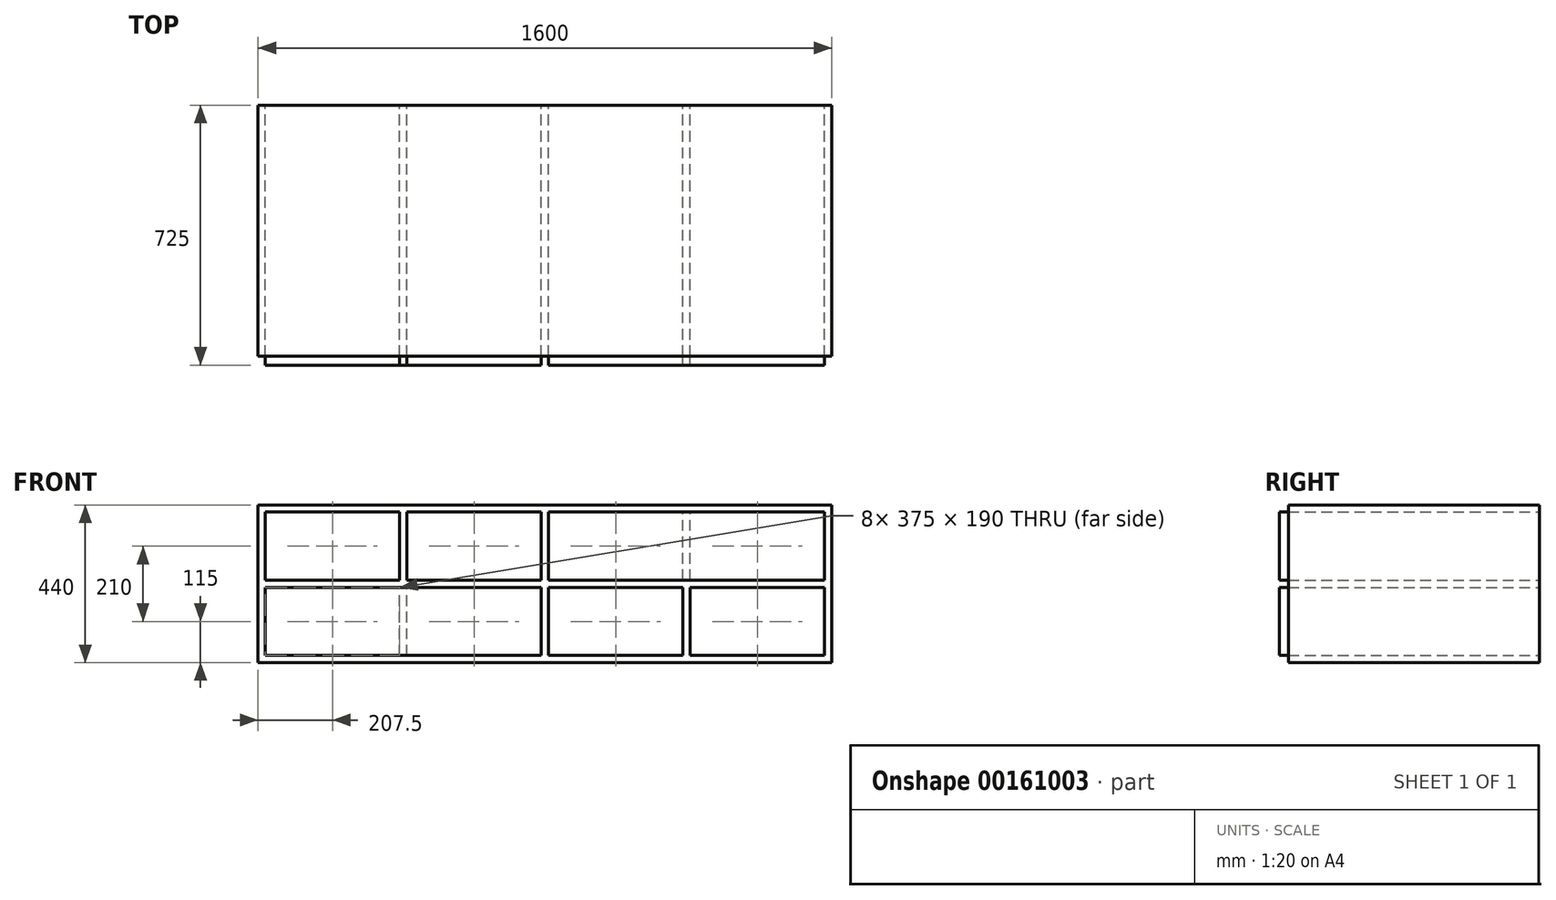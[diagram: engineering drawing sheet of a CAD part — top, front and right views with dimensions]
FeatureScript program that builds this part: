
annotation { "Feature Type Name" : "Feature", "Feature Type Description" : "" }
export const myFeature = defineFeature(function(context is Context, id is Id, definition is map)
    precondition{}
    {
        {
            var Q0;
            Q0=qCreatedBy(makeId("Front.planeOp"),FACE);
            var sketch = newSketch(context, id + "F0", { "sketchPlane" : qUnion([Q0])});
            skLineSegment(sketch, "E0.bottom", {"start": v(800, -220) * mm, "end": v(-800, -220) * mm});
            skLineSegment(sketch, "E0.top", {"start": v(800, 220) * mm, "end": v(-800, 220) * mm});
            skLineSegment(sketch, "E0.left", {"start": v(800, -220) * mm, "end": v(800, 220) * mm});
            skLineSegment(sketch, "E0.right", {"start": v(-800, -220) * mm, "end": v(-800, 220) * mm});
            skPoint(sketch, "E0.middle", {"position": v(0, 0) * mm});
            skLineSegment(sketch, "E1", {"start": v(-800, 105) * mm, "end": v(-780, 105) * mm, "construction": true});
            skLineSegment(sketch, "E2", {"start": v(-405, 105) * mm, "end": v(-385, 105) * mm, "construction": true});
            skLineSegment(sketch, "E3", {"start": v(-10, 105) * mm, "end": v(10, 105) * mm, "construction": true});
            skLineSegment(sketch, "E4", {"start": v(385, 105) * mm, "end": v(405, 105) * mm, "construction": true});
            skLineSegment(sketch, "E5", {"start": v(780, 105) * mm, "end": v(800, 105) * mm, "construction": true});
            skLineSegment(sketch, "E6", {"start": v(-800, -105) * mm, "end": v(-780, -105) * mm, "construction": true});
            skLineSegment(sketch, "E7", {"start": v(-405, -105) * mm, "end": v(-385, -105) * mm, "construction": true});
            skLineSegment(sketch, "E8", {"start": v(-10, -105) * mm, "end": v(10, -105) * mm, "construction": true});
            skLineSegment(sketch, "E9", {"start": v(385, -105) * mm, "end": v(405, -105) * mm, "construction": true});
            skLineSegment(sketch, "E10", {"start": v(780, -105) * mm, "end": v(800, -105) * mm, "construction": true});
            skLineSegment(sketch, "E11", {"start": v(-592.5, 220) * mm, "end": v(-592.5, 200) * mm, "construction": true});
            skLineSegment(sketch, "E12", {"start": v(-592.5, 10) * mm, "end": v(-592.5, -10) * mm, "construction": true});
            skLineSegment(sketch, "E13", {"start": v(-592.5, -200) * mm, "end": v(-592.5, -220) * mm, "construction": true});
            skLineSegment(sketch, "E14", {"start": v(-197.5, 220) * mm, "end": v(-197.5, 200) * mm, "construction": true});
            skLineSegment(sketch, "E15", {"start": v(-197.5, 10) * mm, "end": v(-197.5, -10) * mm, "construction": true});
            skLineSegment(sketch, "E16", {"start": v(-197.5, -200) * mm, "end": v(-197.5, -220) * mm, "construction": true});
            skLineSegment(sketch, "E17", {"start": v(197.5, 220) * mm, "end": v(197.5, 200) * mm, "construction": true});
            skLineSegment(sketch, "E18", {"start": v(197.5, 10) * mm, "end": v(197.5, -10) * mm, "construction": true});
            skLineSegment(sketch, "E19", {"start": v(197.5, -200) * mm, "end": v(197.5, -220) * mm, "construction": true});
            skLineSegment(sketch, "E20", {"start": v(592.5, 220) * mm, "end": v(592.5, 200) * mm, "construction": true});
            skLineSegment(sketch, "E21", {"start": v(592.5, 10) * mm, "end": v(592.5, -10) * mm, "construction": true});
            skLineSegment(sketch, "E22", {"start": v(592.5, -200) * mm, "end": v(592.5, -220) * mm, "construction": true});
            skLineSegment(sketch, "E23.bottom", {"start": v(-405, 10) * mm, "end": v(-780, 10) * mm});
            skLineSegment(sketch, "E23.top", {"start": v(-405, 200) * mm, "end": v(-780, 200) * mm});
            skLineSegment(sketch, "E23.left", {"start": v(-405, 10) * mm, "end": v(-405, 200) * mm});
            skLineSegment(sketch, "E23.right", {"start": v(-780, 10) * mm, "end": v(-780, 200) * mm});
            skPoint(sketch, "E23.middle", {"position": v(-592.5, 105) * mm});
            skLineSegment(sketch, "E24.bottom", {"start": v(-10, 10) * mm, "end": v(-385, 10) * mm});
            skLineSegment(sketch, "E24.top", {"start": v(-10, 200) * mm, "end": v(-385, 200) * mm});
            skLineSegment(sketch, "E24.left", {"start": v(-10, 10) * mm, "end": v(-10, 200) * mm});
            skLineSegment(sketch, "E24.right", {"start": v(-385, 10) * mm, "end": v(-385, 200) * mm});
            skPoint(sketch, "E24.middle", {"position": v(-197.5, 105) * mm});
            skLineSegment(sketch, "E25.bottom", {"start": v(385, 10) * mm, "end": v(10, 10) * mm});
            skLineSegment(sketch, "E25.top", {"start": v(385, 200) * mm, "end": v(10, 200) * mm});
            skLineSegment(sketch, "E25.left", {"start": v(385, 10) * mm, "end": v(385, 200) * mm});
            skLineSegment(sketch, "E25.right", {"start": v(10, 10) * mm, "end": v(10, 200) * mm});
            skPoint(sketch, "E25.middle", {"position": v(197.5, 105) * mm});
            skLineSegment(sketch, "E26.bottom", {"start": v(780, 10) * mm, "end": v(405, 10) * mm});
            skLineSegment(sketch, "E26.top", {"start": v(780, 200) * mm, "end": v(405, 200) * mm});
            skLineSegment(sketch, "E26.left", {"start": v(780, 10) * mm, "end": v(780, 200) * mm});
            skLineSegment(sketch, "E26.right", {"start": v(405, 10) * mm, "end": v(405, 200) * mm});
            skPoint(sketch, "E26.middle", {"position": v(592.5, 105) * mm});
            skLineSegment(sketch, "E27.bottom", {"start": v(-405, -200) * mm, "end": v(-780, -200) * mm});
            skLineSegment(sketch, "E27.top", {"start": v(-405, -10) * mm, "end": v(-780, -10) * mm});
            skLineSegment(sketch, "E27.left", {"start": v(-405, -200) * mm, "end": v(-405, -10) * mm});
            skLineSegment(sketch, "E27.right", {"start": v(-780, -200) * mm, "end": v(-780, -10) * mm});
            skPoint(sketch, "E27.middle", {"position": v(-592.5, -105) * mm});
            skLineSegment(sketch, "E28.bottom", {"start": v(-10, -200) * mm, "end": v(-385, -200) * mm});
            skLineSegment(sketch, "E28.top", {"start": v(-10, -10) * mm, "end": v(-385, -10) * mm});
            skLineSegment(sketch, "E28.left", {"start": v(-10, -200) * mm, "end": v(-10, -10) * mm});
            skLineSegment(sketch, "E28.right", {"start": v(-385, -200) * mm, "end": v(-385, -10) * mm});
            skPoint(sketch, "E28.middle", {"position": v(-197.5, -105) * mm});
            skLineSegment(sketch, "E29.bottom", {"start": v(385, -200) * mm, "end": v(10, -200) * mm});
            skLineSegment(sketch, "E29.top", {"start": v(385, -10) * mm, "end": v(10, -10) * mm});
            skLineSegment(sketch, "E29.left", {"start": v(385, -200) * mm, "end": v(385, -10) * mm});
            skLineSegment(sketch, "E29.right", {"start": v(10, -200) * mm, "end": v(10, -10) * mm});
            skPoint(sketch, "E29.middle", {"position": v(197.5, -105) * mm});
            skLineSegment(sketch, "E30.bottom", {"start": v(780, -200) * mm, "end": v(405, -200) * mm});
            skLineSegment(sketch, "E30.top", {"start": v(780, -10) * mm, "end": v(405, -10) * mm});
            skLineSegment(sketch, "E30.left", {"start": v(780, -200) * mm, "end": v(780, -10) * mm});
            skLineSegment(sketch, "E30.right", {"start": v(405, -200) * mm, "end": v(405, -10) * mm});
            skPoint(sketch, "E30.middle", {"position": v(592.5, -105) * mm});
            skLineSegment(sketch, "E31", {"start": v(0, 105) * mm, "end": v(0, 0) * mm, "construction": true});
            skLineSegment(sketch, "E32", {"start": v(0, 0) * mm, "end": v(0, -105) * mm, "construction": true});
            skSolve(sketch);
        }
        {
            var Q0;
            Q0 = qSketchRegion(id + "F0", true);
            extrude(context, id + "F1", {"entities" : qUnion([Q0]), "depth" : 700 * mm});
        }
        {
            var Q0;
            Q0=makeQuery(id+"F1.opExtrude","CAP_FACE",FACE,{"disambiguationData":[OSD([sQuery(id+"F0.wireOp",EDGE,"E0.bottom"),sQuery(id+"F0.wireOp",EDGE,"E0.top"),sQuery(id+"F0.wireOp",EDGE,"E0.left"),sQuery(id+"F0.wireOp",EDGE,"E0.right"),sQuery(id+"F0.wireOp",EDGE,"E23.bottom"),sQuery(id+"F0.wireOp",EDGE,"E23.top"),sQuery(id+"F0.wireOp",EDGE,"E23.left"),sQuery(id+"F0.wireOp",EDGE,"E23.right"),sQuery(id+"F0.wireOp",EDGE,"E24.bottom"),sQuery(id+"F0.wireOp",EDGE,"E24.top"),sQuery(id+"F0.wireOp",EDGE,"E24.left"),sQuery(id+"F0.wireOp",EDGE,"E24.right"),sQuery(id+"F0.wireOp",EDGE,"E25.bottom"),sQuery(id+"F0.wireOp",EDGE,"E25.top"),sQuery(id+"F0.wireOp",EDGE,"E25.left"),sQuery(id+"F0.wireOp",EDGE,"E25.right"),sQuery(id+"F0.wireOp",EDGE,"E26.bottom"),sQuery(id+"F0.wireOp",EDGE,"E26.top"),sQuery(id+"F0.wireOp",EDGE,"E26.left"),sQuery(id+"F0.wireOp",EDGE,"E26.right"),sQuery(id+"F0.wireOp",EDGE,"E27.bottom"),sQuery(id+"F0.wireOp",EDGE,"E27.top"),sQuery(id+"F0.wireOp",EDGE,"E27.left"),sQuery(id+"F0.wireOp",EDGE,"E27.right"),sQuery(id+"F0.wireOp",EDGE,"E28.bottom"),sQuery(id+"F0.wireOp",EDGE,"E28.top"),sQuery(id+"F0.wireOp",EDGE,"E28.left"),sQuery(id+"F0.wireOp",EDGE,"E28.right"),sQuery(id+"F0.wireOp",EDGE,"E29.bottom"),sQuery(id+"F0.wireOp",EDGE,"E29.top"),sQuery(id+"F0.wireOp",EDGE,"E29.left"),sQuery(id+"F0.wireOp",EDGE,"E29.right"),sQuery(id+"F0.wireOp",EDGE,"E30.bottom"),sQuery(id+"F0.wireOp",EDGE,"E30.top"),sQuery(id+"F0.wireOp",EDGE,"E30.left"),sQuery(id+"F0.wireOp",EDGE,"E30.right")])],"isStart":false});
            var sketch = newSketch(context, id + "F2", { "sketchPlane" : qUnion([Q0])});
            skLineSegment(sketch, "E33.0", {"start": v(-405, 200) * mm, "end": v(-780, 200) * mm});
            skLineSegment(sketch, "E34.0", {"start": v(-780, 10) * mm, "end": v(-780, 200) * mm});
            skLineSegment(sketch, "E35.0", {"start": v(-405, 10) * mm, "end": v(-780, 10) * mm});
            skLineSegment(sketch, "E36.0", {"start": v(-405, 10) * mm, "end": v(-405, 200) * mm});
            skLineSegment(sketch, "E37.0", {"start": v(-385, 10) * mm, "end": v(-385, 200) * mm});
            skLineSegment(sketch, "E38.0", {"start": v(-10, 200) * mm, "end": v(-385, 200) * mm});
            skLineSegment(sketch, "E39.0", {"start": v(-10, 10) * mm, "end": v(-10, 200) * mm});
            skLineSegment(sketch, "E40.0", {"start": v(-10, 10) * mm, "end": v(-385, 10) * mm});
            skLineSegment(sketch, "E41.0", {"start": v(385, -10) * mm, "end": v(10, -10) * mm});
            skLineSegment(sketch, "E42.0", {"start": v(10, -200) * mm, "end": v(10, -10) * mm});
            skLineSegment(sketch, "E43.0", {"start": v(385, -200) * mm, "end": v(10, -200) * mm});
            skLineSegment(sketch, "E44.0", {"start": v(385, -200) * mm, "end": v(385, -10) * mm});
            skLineSegment(sketch, "E45.0", {"start": v(405, -200) * mm, "end": v(405, -10) * mm});
            skLineSegment(sketch, "E46.0", {"start": v(780, -10) * mm, "end": v(405, -10) * mm});
            skLineSegment(sketch, "E47.0", {"start": v(780, -200) * mm, "end": v(405, -200) * mm});
            skLineSegment(sketch, "E48.0", {"start": v(780, -200) * mm, "end": v(780, -10) * mm});
            skLineSegment(sketch, "E49.0", {"start": v(10, 10) * mm, "end": v(10, 200) * mm});
            skLineSegment(sketch, "E50.0", {"start": v(780, 10) * mm, "end": v(780, 200) * mm});
            skLineSegment(sketch, "E51.0", {"start": v(-10, -200) * mm, "end": v(-10, -10) * mm});
            skLineSegment(sketch, "E52.0", {"start": v(-780, -200) * mm, "end": v(-780, -10) * mm});
            skLineSegment(sketch, "E53", {"start": v(-780, -10) * mm, "end": v(-10, -10) * mm});
            skLineSegment(sketch, "E54", {"start": v(-10, -200) * mm, "end": v(-780, -200) * mm});
            skLineSegment(sketch, "E55", {"start": v(10, 200) * mm, "end": v(780, 200) * mm});
            skLineSegment(sketch, "E56", {"start": v(780, 10) * mm, "end": v(10, 10) * mm});
            skSolve(sketch);
        }
        {
            var Q0;
            Q0 = qSketchRegion(id + "F2", true);
            extrude(context, id + "F3", {"entities" : qUnion([Q0]), "depth" : 25 * mm});
        }
    });
